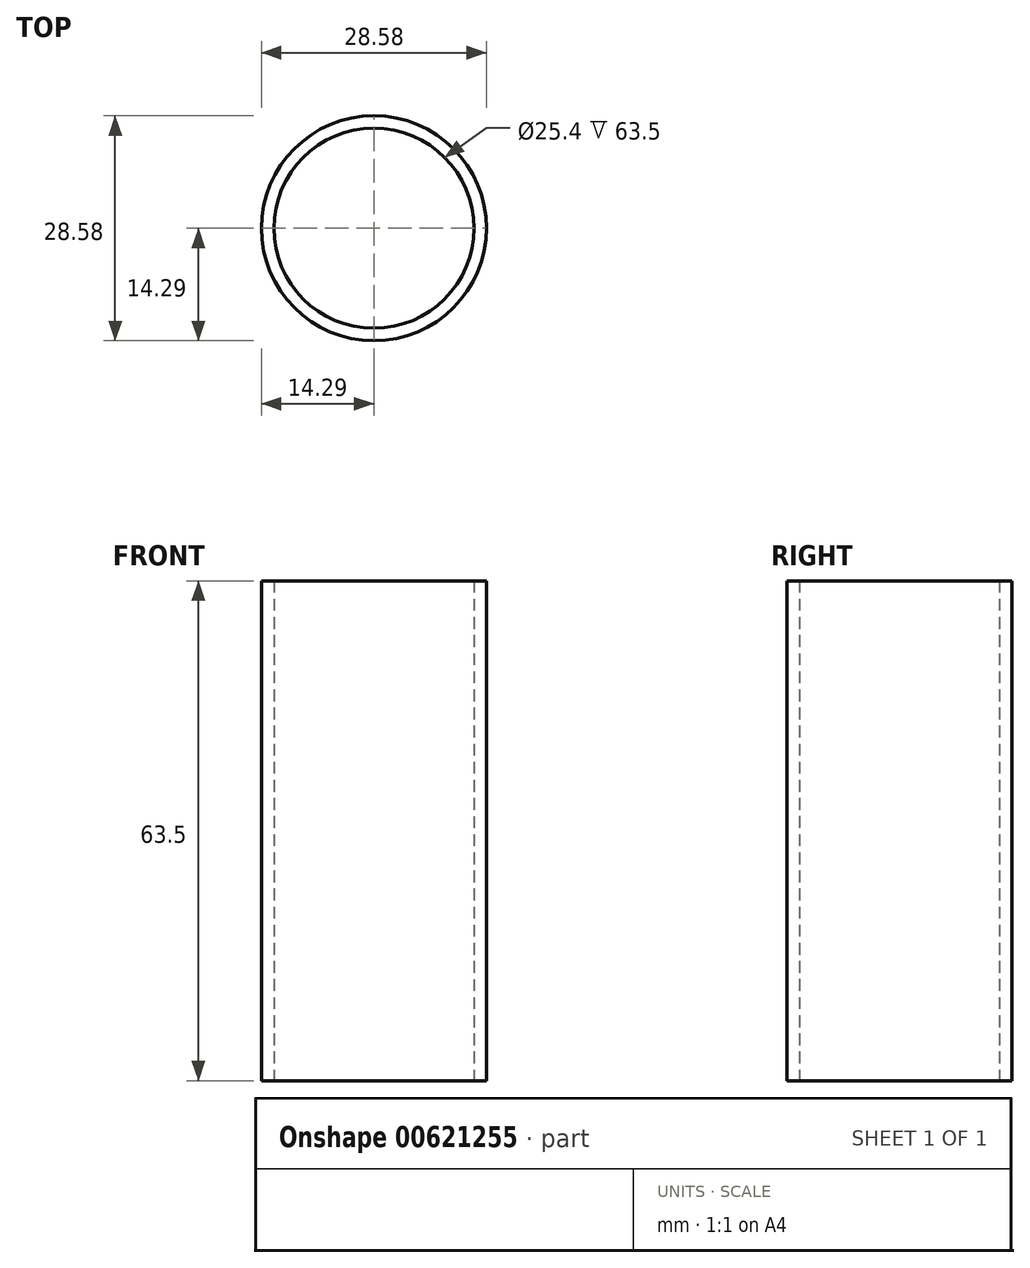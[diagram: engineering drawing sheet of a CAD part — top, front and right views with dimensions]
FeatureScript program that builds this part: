
annotation { "Feature Type Name" : "Feature", "Feature Type Description" : "" }
export const myFeature = defineFeature(function(context is Context, id is Id, definition is map)
    precondition{}
    {
        {
            var Q0;
            Q0=qCreatedBy(makeId("Top.planeOp"),FACE);
            var sketch = newSketch(context, id + "F0", { "sketchPlane" : qUnion([Q0])});
            skLineSegment(sketch, "E0", {"start": v(0, 0) * mm, "end": v(12.7, 0) * mm});
            skCircle(sketch, "E1", {"center": v(0, 0) * mm, "radius": 12.7 * mm});
            skCircle(sketch, "E2.0", {"center": v(0, 0) * mm, "radius": 14.29 * mm});
            skSolve(sketch);
        }
        {
            var Q0;
            Q0=qCreatedBy(makeId("Top.planeOp"),FACE);
            var sketch = newSketch(context, id + "F1", { "sketchPlane" : qUnion([Q0])});
            skSolve(sketch);
        }
        {
            var Q0;
            Q0=qSketchRegion(id+"F1",true);
            var Q1;
            Q1=makeQuery(id+"F0.imprint","IMPRINT",FACE,{"disambiguationData":[TD([[makeQuery(id+"F0.imprint","IMPRINT",EDGE,{"derivedFrom":sQuery(id+"F0.wireOp",EDGE,"E1")}),-1.0]])]});
            extrude(context, id + "F2", {"entities" : qUnion([Q0, Q1]), "depth" : 63.5 * mm, "offsetDistance" : 25.4 * mm});
        }
    });
